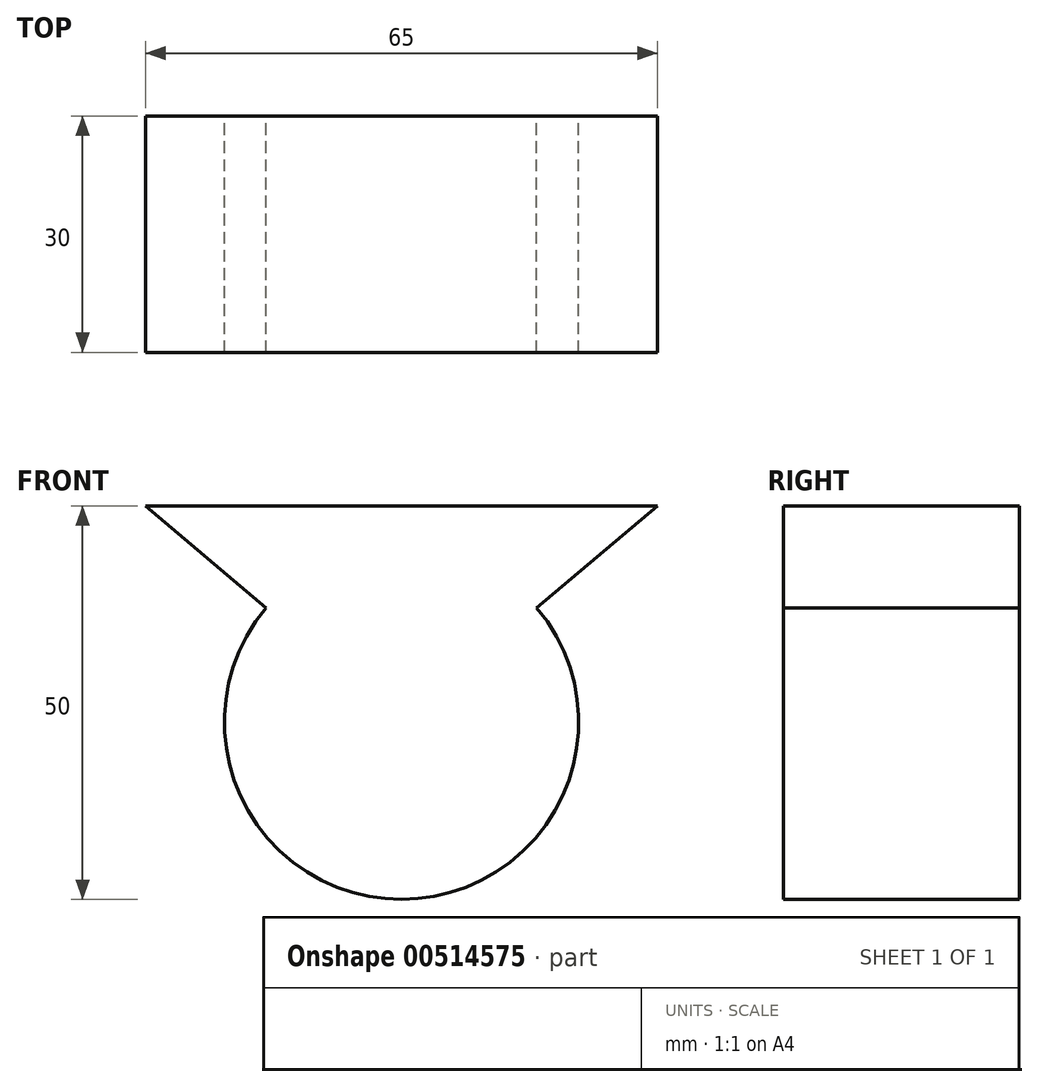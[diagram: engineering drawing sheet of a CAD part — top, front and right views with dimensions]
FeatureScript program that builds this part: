
annotation { "Feature Type Name" : "Feature", "Feature Type Description" : "" }
export const myFeature = defineFeature(function(context is Context, id is Id, definition is map)
    precondition{}
    {
        {
            var Q0;
            Q0=qCreatedBy(makeId("Front.planeOp"),FACE);
            var sketch = newSketch(context, id + "F0", { "sketchPlane" : qUnion([Q0])});
            skLineSegment(sketch, "E0", {"start": v(0, 0) * mm, "end": v(65, 0) * mm});
            skLineSegment(sketch, "E1", {"start": v(65, 0) * mm, "end": v(49.68, -12.97) * mm});
            skLineSegment(sketch, "E2", {"start": v(15.32, -12.97) * mm, "end": v(0, 0) * mm});
            skArc(sketch, "E3", {"start": v(15.32, -12.97) * mm, "mid": v(32.5, -50) * mm, "end": v(49.68, -12.97) * mm});
            skLineSegment(sketch, "E4", {"start": v(15.32, -12.97) * mm, "end": v(32.5, -27.5) * mm, "construction": true});
            skLineSegment(sketch, "E5", {"start": v(49.68, -12.97) * mm, "end": v(32.5, -27.5) * mm, "construction": true});
            skLineSegment(sketch, "E6", {"start": v(32.5, -27.5) * mm, "end": v(32.5, 0) * mm, "construction": true});
            skSolve(sketch);
        }
        {
            var Q0;
            Q0 = qSketchRegion(id + "F0", true);
            extrude(context, id + "F1", {"entities" : qUnion([Q0]), "depth" : 30 * mm, "offsetDistance" : 25 * mm});
        }
    });
